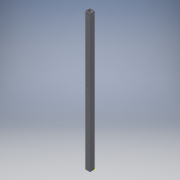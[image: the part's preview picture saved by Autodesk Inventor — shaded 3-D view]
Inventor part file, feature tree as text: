
AUTODESK INVENTOR PART (.ipt)
format: ipt  version: 2016 (Build 200138000, 138)  size: 118,784 bytes
history: native  units: in
note: dims shown in document units (in); Inventor stores cm internally (conversion verified against a paired STEP export)
features: sketch x4, extrude x3
ambient origin geometry x8: Origin, YZ Plane, XZ Plane, XY Plane, X Axis, Y Axis, Z Axis, Center Point
bodies: Solid1 (feature_tree)
feature tree (7):
  extrude  "Extrusion1"  Depth=1.0in
  extrude  "Extrusion2"  Depth=29.0in TaperAngle=0.0deg
  sketch  "Sketch3"  dims[d5=0.5in d6=0.5in]
  extrude  "Extrusion3"  Depth=0.5in
  sketch  "Sketch1"  dims[d0=1.0in d1=1.0in]
  sketch  "Sketch2"  dims[d2=0.0625in d3=29.0in d4=0.0in]
  sketch  "Sketch4"  dims[d7=0.5in d8=13.7in d9=1.0in d10=0.0in d11=0.4761in d12=0.313in d13=2.158in d14=0.25in d15=1.0in d16=0.0in]
